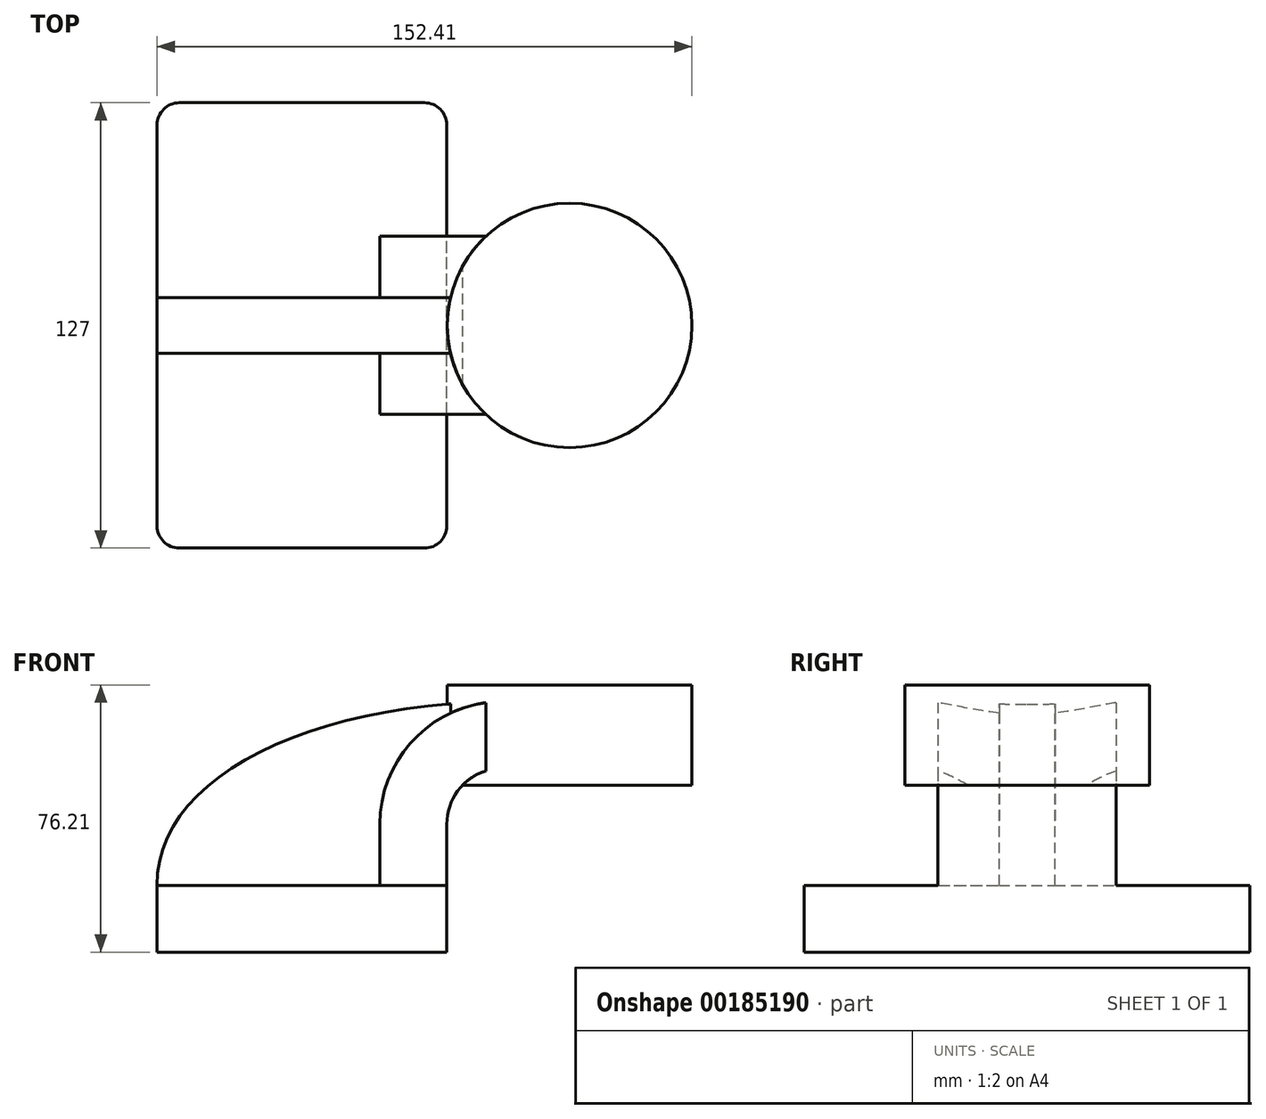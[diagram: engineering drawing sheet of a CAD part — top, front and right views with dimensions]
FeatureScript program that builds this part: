
annotation { "Feature Type Name" : "Feature", "Feature Type Description" : "" }
export const myFeature = defineFeature(function(context is Context, id is Id, definition is map)
    precondition{}
    {
        {
            var Q0;
            Q0=qCreatedBy(makeId("Front.planeOp"),FACE);
            var sketch = newSketch(context, id + "F0", { "sketchPlane" : qUnion([Q0])});
            skLineSegment(sketch, "E0.bottom", {"start": v(41.27, 9.53) * mm, "end": v(-41.28, 9.53) * mm});
            skLineSegment(sketch, "E0.top", {"start": v(41.28, -9.52) * mm, "end": v(-41.27, -9.52) * mm});
            skLineSegment(sketch, "E0.left", {"start": v(41.28, 9.53) * mm, "end": v(41.28, -9.52) * mm});
            skLineSegment(sketch, "E0.right", {"start": v(-41.28, 9.53) * mm, "end": v(-41.27, -9.52) * mm});
            skPoint(sketch, "E0.middle", {"position": v(0, 0) * mm});
            skLineSegment(sketch, "E1.bottom", {"start": v(60.32, 66.68) * mm, "end": v(111.13, 66.68) * mm});
            skLineSegment(sketch, "E1.top", {"start": v(60.33, 38.1) * mm, "end": v(111.13, 38.1) * mm});
            skLineSegment(sketch, "E1.left", {"start": v(60.33, 66.68) * mm, "end": v(60.33, 38.1) * mm});
            skLineSegment(sketch, "E1.right", {"start": v(111.13, 66.68) * mm, "end": v(111.13, 38.1) * mm});
            skPoint(sketch, "E1.middle", {"position": v(85.73, 52.39) * mm});
            skLineSegment(sketch, "E2", {"start": v(41.27, 9.53) * mm, "end": v(41.27, 27) * mm});
            skArc(sketch, "E3", {"start": v(41.27, 27) * mm, "mid": v(45.92, 38.23) * mm, "end": v(57.15, 42.88) * mm});
            skLineSegment(sketch, "E4", {"start": v(57.15, 42.88) * mm, "end": v(76.04, 42.88) * mm});
            skLineSegment(sketch, "E5.0", {"start": v(57.15, 61.93) * mm, "end": v(76.04, 61.93) * mm});
            skArc(sketch, "E5.1", {"start": v(22.23, 27) * mm, "mid": v(32.45, 51.7) * mm, "end": v(57.15, 61.93) * mm});
            skLineSegment(sketch, "E5.2", {"start": v(22.22, 9.53) * mm, "end": v(22.22, 27) * mm});
            skLineSegment(sketch, "E6", {"start": v(76.27, 38.1) * mm, "end": v(76.27, 66.68) * mm});
            skFitSpline(sketch, "E7", {"points": [v(-41.28, 9.53) * mm, v(57.15, 61.93) * mm], "startDerivative": vector(-1.41, 89.27) * mm, "endDerivative": vector(171.45, 2.08) * mm});
            skSolve(sketch);
        }
        {
            var Q0;
            Q0=makeQuery(id+"F0.imprint","IMPRINT",FACE,{"disambiguationData":[TD([[makeQuery(id+"F0.imprint","IMPRINT",EDGE,{"derivedFrom":sQuery(id+"F0.wireOp",EDGE,"E0.top")}),-1.0]])]});
            extrude(context, id + "F1", {"entities" : qUnion([Q0]), "endBound" : BoundingType.SYMMETRIC, "depth" : 127 * mm});
        }
        {
            var Q0;
            {var subQ1=sQuery(id+"F0.wireOp",EDGE,"E2");Q0=makeQuery(id+"F0.imprint","IMPRINT",FACE,{"disambiguationData":[TD([[makeQuery(id+"F0.imprint","IMPRINT",EDGE,{"derivedFrom":subQ1}),1.0]])]});}
            extrude(context, id + "F2", {"entities" : qUnion([Q0]), "operationType" : NewBodyOperationType.ADD, "endBound" : BoundingType.SYMMETRIC, "depth" : 50.8 * mm});
        }
        {
            var Q0;
            {var subQ3=sQuery(id+"F0.wireOp",EDGE,"E5.2");Q0=makeQuery(id+"F0.imprint","IMPRINT",FACE,{"disambiguationData":[TD([[makeQuery(id+"F0.imprint","IMPRINT",EDGE,{"derivedFrom":subQ3}),1.0]])]});}
            extrude(context, id + "F3", {"entities" : qUnion([Q0]), "operationType" : NewBodyOperationType.ADD, "endBound" : BoundingType.SYMMETRIC, "depth" : 15.88 * mm});
        }
        {
            var Q0;
            {var subQ0=sQuery(id+"F0.wireOp",EDGE,"E1.right");Q0=makeQuery(id+"F0.imprint","IMPRINT",FACE,{"disambiguationData":[TD([[makeQuery(id+"F0.imprint","IMPRINT",EDGE,{"derivedFrom":subQ0}),-1.0]])]});}
            var Q1;
            Q1=sQuery(id+"F0.wireOp",EDGE,"E6");
            revolve(context, id + "F4", {"operationType" : NewBodyOperationType.ADD, "entities" : qUnion([Q0]), "axis" : qUnion([Q1]), "revolveType" : RevolveType.FULL});
        }
        {
            var Q0;
            Q0=makeQuery(id+"F1.opExtrude","CAP_EDGE",EDGE,{"disambiguationData":[OSD([sQuery(id+"F0.wireOp",EDGE,"E0.right")])],"isStart":false});
            var Q1;
            Q1=makeQuery(id+"F1.opExtrude","CAP_EDGE",EDGE,{"disambiguationData":[OSD([sQuery(id+"F0.wireOp",EDGE,"E0.left")])],"isStart":false});
            var Q2;
            Q2=makeQuery(id+"F1.opExtrude","CAP_EDGE",EDGE,{"disambiguationData":[OSD([sQuery(id+"F0.wireOp",EDGE,"E0.left")])],"isStart":true});
            var Q3;
            Q3=makeQuery(id+"F1.opExtrude","CAP_EDGE",EDGE,{"disambiguationData":[OSD([sQuery(id+"F0.wireOp",EDGE,"E0.right")])],"isStart":true});
            fillet(context, id + "F5", {"entities" : qUnion([Q0, Q1, Q2, Q3]), "radius" : 6.35 * mm, "tangentPropagation" : true, "allowEdgeOverflow" : false});
        }
    });
